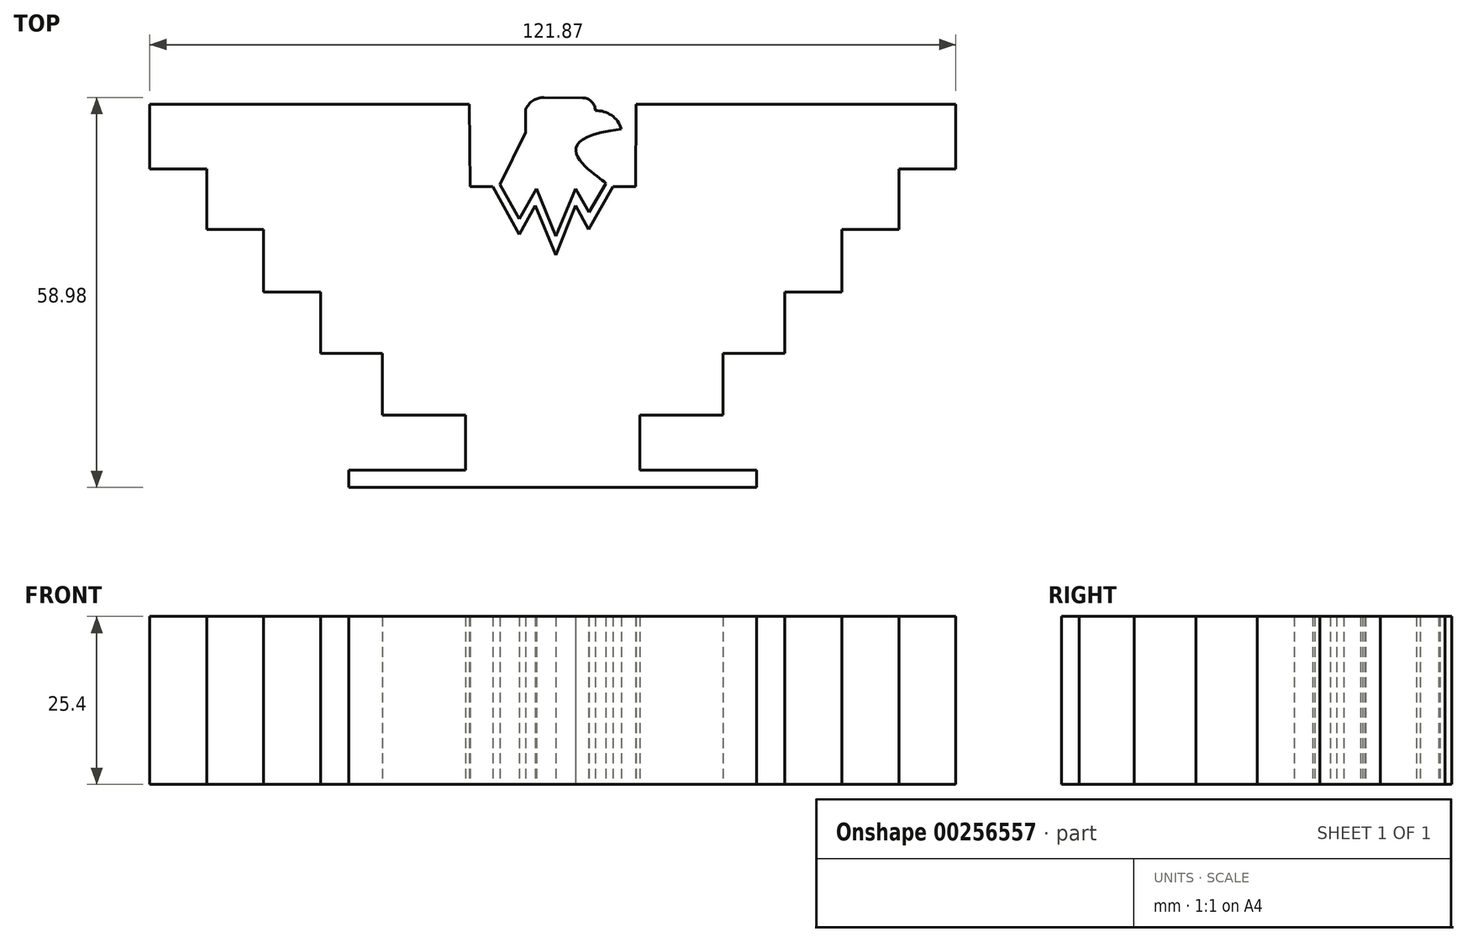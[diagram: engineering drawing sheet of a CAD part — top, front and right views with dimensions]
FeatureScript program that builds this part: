
annotation { "Feature Type Name" : "Feature", "Feature Type Description" : "" }
export const myFeature = defineFeature(function(context is Context, id is Id, definition is map)
    precondition{}
    {
        {
            var Q0;
            Q0=qCreatedBy(makeId("Top.planeOp"),FACE);
            var sketch = newSketch(context, id + "F0", { "sketchPlane" : qUnion([Q0])});
            skLineSegment(sketch, "E0", {"start": v(-28.35, -24.27) * mm, "end": v(33.33, -24.27) * mm});
            skLineSegment(sketch, "E1", {"start": v(33.33, -24.27) * mm, "end": v(33.33, -21.61) * mm});
            skLineSegment(sketch, "E2", {"start": v(33.33, -21.61) * mm, "end": v(15.68, -21.61) * mm});
            skLineSegment(sketch, "E3", {"start": v(15.68, -21.61) * mm, "end": v(15.68, -13.32) * mm});
            skLineSegment(sketch, "E4", {"start": v(15.68, -13.32) * mm, "end": v(28.23, -13.32) * mm});
            skLineSegment(sketch, "E5", {"start": v(28.23, -13.32) * mm, "end": v(28.23, -3.96) * mm});
            skLineSegment(sketch, "E6", {"start": v(28.23, -3.96) * mm, "end": v(37.59, -3.96) * mm});
            skLineSegment(sketch, "E7", {"start": v(37.59, -3.96) * mm, "end": v(37.59, 5.3) * mm});
            skLineSegment(sketch, "E8", {"start": v(37.59, 5.3) * mm, "end": v(46.2, 5.3) * mm});
            skLineSegment(sketch, "E9", {"start": v(46.2, 5.3) * mm, "end": v(46.2, 14.76) * mm});
            skLineSegment(sketch, "E10", {"start": v(46.2, 14.76) * mm, "end": v(54.81, 14.76) * mm});
            skLineSegment(sketch, "E11", {"start": v(54.81, 14.76) * mm, "end": v(54.81, 23.9) * mm});
            skLineSegment(sketch, "E12", {"start": v(54.81, 23.9) * mm, "end": v(63.43, 23.9) * mm});
            skLineSegment(sketch, "E13", {"start": v(63.43, 23.9) * mm, "end": v(63.43, 33.69) * mm});
            skLineSegment(sketch, "E14", {"start": v(63.43, 33.69) * mm, "end": v(15.1, 33.69) * mm});
            skLineSegment(sketch, "E15", {"start": v(15.1, 33.69) * mm, "end": v(15, 21.21) * mm});
            skLineSegment(sketch, "E16", {"start": v(15, 21.21) * mm, "end": v(11.6, 21.21) * mm});
            skPoint(sketch, "E17", {"position": v(2.5, -24.27) * mm});
            skLineSegment(sketch, "E18", {"start": v(2.5, -24.27) * mm, "end": v(2.5, 43.83) * mm, "construction": true});
            skLineSegment(sketch, "E19.MirrorCS", {"start": v(-10, 21.21) * mm, "end": v(-6.6, 21.21) * mm});
            skLineSegment(sketch, "E20.MirrorCS", {"start": v(-10.11, 33.69) * mm, "end": v(-10, 21.21) * mm});
            skLineSegment(sketch, "E21.MirrorCS", {"start": v(-58.44, 33.69) * mm, "end": v(-10.11, 33.69) * mm});
            skLineSegment(sketch, "E22.MirrorCS", {"start": v(-58.44, 23.9) * mm, "end": v(-58.44, 33.69) * mm});
            skLineSegment(sketch, "E23.MirrorCS", {"start": v(-49.83, 23.9) * mm, "end": v(-58.44, 23.9) * mm});
            skLineSegment(sketch, "E24.MirrorCS", {"start": v(-49.83, 14.76) * mm, "end": v(-49.83, 23.9) * mm});
            skLineSegment(sketch, "E25.MirrorCS", {"start": v(-41.22, 14.76) * mm, "end": v(-49.83, 14.76) * mm});
            skLineSegment(sketch, "E26.MirrorCS", {"start": v(-41.22, 5.3) * mm, "end": v(-41.22, 14.76) * mm});
            skLineSegment(sketch, "E27.MirrorCS", {"start": v(-32.6, 5.3) * mm, "end": v(-41.22, 5.3) * mm});
            skLineSegment(sketch, "E28.MirrorCS", {"start": v(-32.6, -3.96) * mm, "end": v(-32.6, 5.3) * mm});
            skLineSegment(sketch, "E29.MirrorCS", {"start": v(-23.24, -3.96) * mm, "end": v(-32.6, -3.96) * mm});
            skLineSegment(sketch, "E30.MirrorCS", {"start": v(-10.7, -13.32) * mm, "end": v(-23.24, -13.32) * mm});
            skLineSegment(sketch, "E31.MirrorCS", {"start": v(-10.7, -21.61) * mm, "end": v(-10.7, -13.32) * mm});
            skLineSegment(sketch, "E32.MirrorCS", {"start": v(-23.24, -13.32) * mm, "end": v(-23.24, -3.96) * mm});
            skLineSegment(sketch, "E33.MirrorCS", {"start": v(-28.35, -21.61) * mm, "end": v(-10.7, -21.61) * mm});
            skLineSegment(sketch, "E34.MirrorCS", {"start": v(-28.35, -24.27) * mm, "end": v(-28.35, -21.61) * mm});
            skLineSegment(sketch, "E35", {"start": v(-6.6, 21.21) * mm, "end": v(-2.57, 14) * mm});
            skLineSegment(sketch, "E36", {"start": v(-2.57, 14) * mm, "end": v(-0.18, 18.36) * mm});
            skLineSegment(sketch, "E37", {"start": v(-0.18, 18.36) * mm, "end": v(2.97, 10.85) * mm});
            skLineSegment(sketch, "E38", {"start": v(2.97, 10.85) * mm, "end": v(5.93, 18.36) * mm});
            skLineSegment(sketch, "E39", {"start": v(5.93, 18.36) * mm, "end": v(7.88, 14.76) * mm});
            skLineSegment(sketch, "E40", {"start": v(7.88, 14.76) * mm, "end": v(11.6, 21.21) * mm});
            skLineSegment(sketch, "E41", {"start": v(-2.57, 16.35) * mm, "end": v(0, 20.93) * mm});
            skLineSegment(sketch, "E42", {"start": v(0, 20.93) * mm, "end": v(2.97, 13.7) * mm});
            skLineSegment(sketch, "E43", {"start": v(2.97, 13.7) * mm, "end": v(5.93, 20.93) * mm});
            skLineSegment(sketch, "E44", {"start": v(5.93, 20.93) * mm, "end": v(7.94, 17.32) * mm});
            skLineSegment(sketch, "E45", {"start": v(7.94, 17.32) * mm, "end": v(10.54, 21.66) * mm});
            skLineSegment(sketch, "E46", {"start": v(-2.57, 16.35) * mm, "end": v(-5.47, 21.53) * mm});
            skLineSegment(sketch, "E47", {"start": v(-5.47, 21.53) * mm, "end": v(-1.6, 29.38) * mm});
            skLineSegment(sketch, "E48", {"start": v(-1.6, 29.38) * mm, "end": v(-1.6, 32.93) * mm});
            skArc(sketch, "E49", {"start": v(1.14, 34.7) * mm, "mid": v(-0.5, 34.23) * mm, "end": v(-1.6, 32.93) * mm});
            skLineSegment(sketch, "E50", {"start": v(1.14, 34.7) * mm, "end": v(7, 34.65) * mm});
            skArc(sketch, "E51", {"start": v(8.92, 32.7) * mm, "mid": v(8.36, 34.07) * mm, "end": v(7, 34.65) * mm});
            skArc(sketch, "E52", {"start": v(12.85, 29.92) * mm, "mid": v(11.37, 32) * mm, "end": v(8.92, 32.7) * mm});
            skFitSpline(sketch, "E53", {"points": [v(12.85, 29.92) * mm, v(10.54, 21.66) * mm], "startDerivative": vector(-41.41, -4.8) * mm, "endDerivative": vector(0.88, -2.22) * mm});
            skSolve(sketch);
        }
        {
            var Q0;
            Q0 = qSketchRegion(id + "F0", true);
            extrude(context, id + "F1", {"entities" : qUnion([Q0]), "depth" : 25.4 * mm, "offsetDistance" : 25.4 * mm});
        }
    });
